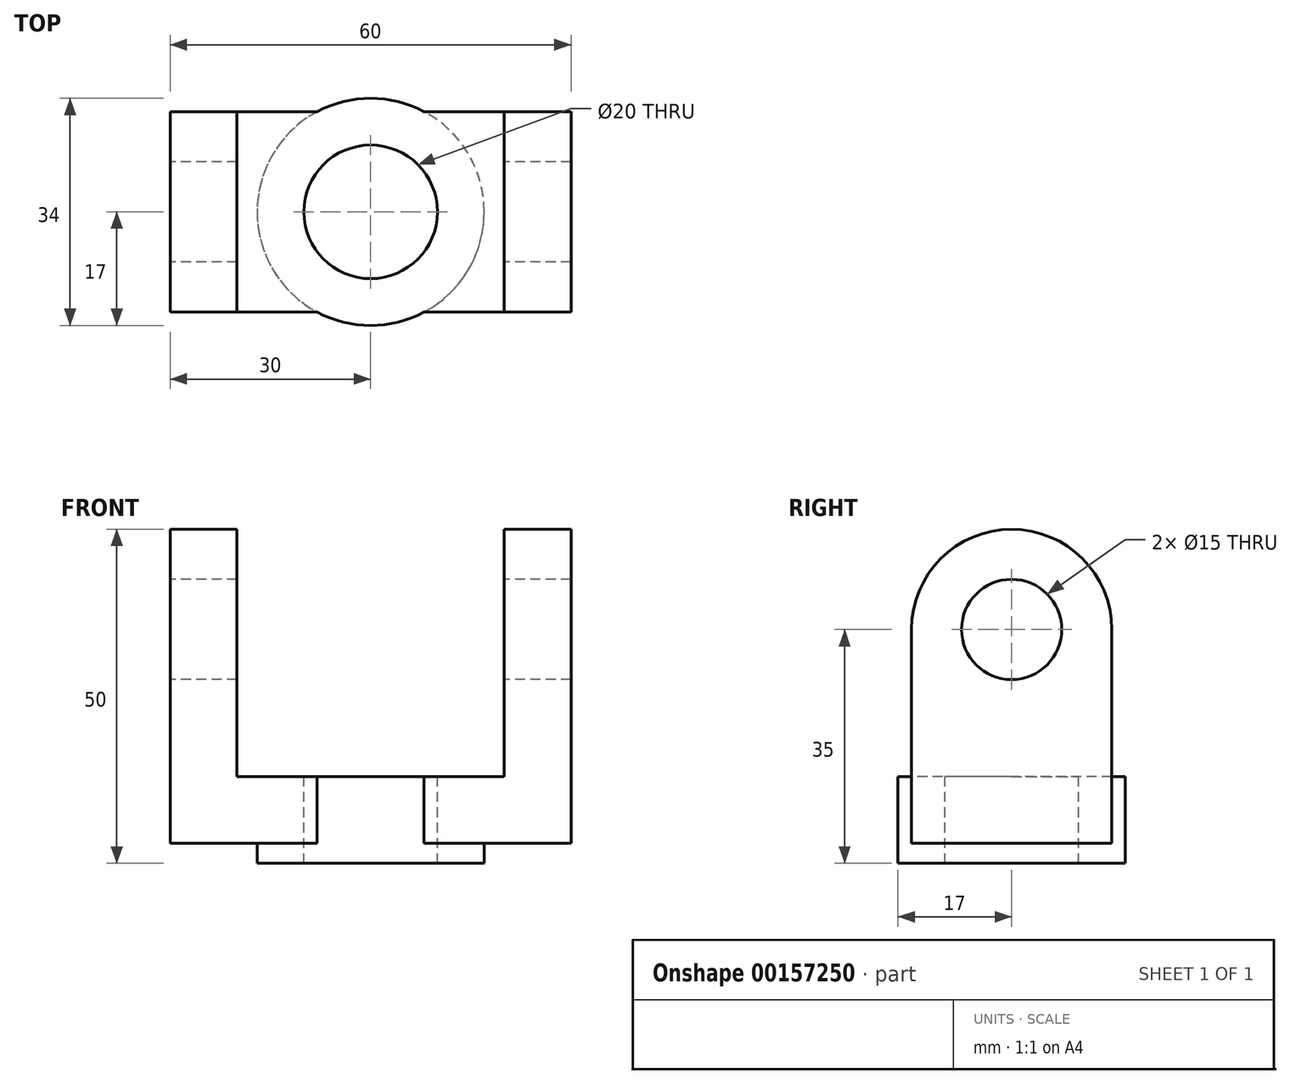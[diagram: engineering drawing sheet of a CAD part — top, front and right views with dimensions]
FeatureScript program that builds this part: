
annotation { "Feature Type Name" : "Feature", "Feature Type Description" : "" }
export const myFeature = defineFeature(function(context is Context, id is Id, definition is map)
    precondition{}
    {
        {
            var Q0;
            Q0=qCreatedBy(makeId("Right.planeOp"),FACE);
            var sketch = newSketch(context, id + "F0", { "sketchPlane" : qUnion([Q0])});
            skLineSegment(sketch, "E0", {"start": v(-15, 0) * mm, "end": v(15, 0) * mm});
            skLineSegment(sketch, "E1", {"start": v(-15, 0) * mm, "end": v(-15, 10) * mm});
            skLineSegment(sketch, "E2", {"start": v(15, 0) * mm, "end": v(15, 10) * mm});
            skLineSegment(sketch, "E3", {"start": v(-15, 10) * mm, "end": v(-15, 32) * mm});
            skLineSegment(sketch, "E4", {"start": v(15, 10) * mm, "end": v(15, 32) * mm});
            skArc(sketch, "E5", {"start": v(15, 32) * mm, "mid": v(0, 47) * mm, "end": v(-15, 32) * mm});
            skCircle(sketch, "E6", {"center": v(0, 32) * mm, "radius": 7.5 * mm});
            skSolve(sketch);
        }
        {
            var Q0;
            Q0 = qSketchRegion(id + "F0", true);
            extrude(context, id + "F1", {"entities" : qUnion([Q0]), "depth" : 60 * mm});
        }
        {
            var Q0;
            Q0=makeQuery(id+"F1.opExtrude","SWEPT_FACE",FACE,{"disambiguationData":[OSD([sQuery(id+"F0.wireOp",EDGE,"E3")])]});
            var sketch = newSketch(context, id + "F2", { "sketchPlane" : qUnion([Q0])});
            skLineSegment(sketch, "E7", {"start": v(10, 82.92) * mm, "end": v(10, 32) * mm});
            skLineSegment(sketch, "E8", {"start": v(10, 32) * mm, "end": v(50, 32) * mm});
            skLineSegment(sketch, "E9", {"start": v(50, 32) * mm, "end": v(50, 85.16) * mm});
            skLineSegment(sketch, "E10", {"start": v(50, 85.16) * mm, "end": v(10, 82.92) * mm});
            skSolve(sketch);
        }
        {
            var Q0;
            Q0 = qSketchRegion(id + "F2", true);
            extrude(context, id + "F3", {"entities" : qUnion([Q0]), "operationType" : NewBodyOperationType.REMOVE, "endBound" : BoundingType.THROUGH_ALL, "oppositeDirection" : true, "depth" : 25 * mm});
        }
        {
            var Q0;
            Q0=makeQuery(id+"F1.opExtrude","SWEPT_FACE",FACE,{"disambiguationData":[OSD([sQuery(id+"F0.wireOp",EDGE,"E1"),sQuery(id+"F0.wireOp",EDGE,"E3")])]});
            var sketch = newSketch(context, id + "F4", { "sketchPlane" : qUnion([Q0])});
            skLineSegment(sketch, "E11", {"start": v(50, 10) * mm, "end": v(50, 32) * mm});
            skLineSegment(sketch, "E12", {"start": v(50, 32) * mm, "end": v(10, 32) * mm});
            skLineSegment(sketch, "E13", {"start": v(10, 32) * mm, "end": v(10, 10) * mm});
            skLineSegment(sketch, "E14", {"start": v(10, 10) * mm, "end": v(50, 10) * mm});
            skSolve(sketch);
        }
        {
            var Q0;
            Q0 = qSketchRegion(id + "F4", true);
            extrude(context, id + "F5", {"entities" : qUnion([Q0]), "operationType" : NewBodyOperationType.REMOVE, "endBound" : BoundingType.THROUGH_ALL, "oppositeDirection" : true, "depth" : 25 * mm});
        }
        {
            var Q0;
            Q0=makeQuery(id+"F5.boolean.opBoolean","COPY",FACE,{"derivedFrom":makeQuery(id+"F5.opExtrude","SWEPT_FACE",FACE,{"disambiguationData":[OSD([sQuery(id+"F4.wireOp",EDGE,"E14")])]})});
            var sketch = newSketch(context, id + "F6", { "sketchPlane" : qUnion([Q0])});
            skCircle(sketch, "E15", {"center": v(30, 0) * mm, "radius": 10 * mm});
            skCircle(sketch, "E16", {"center": v(30, 0) * mm, "radius": 17 * mm});
            skSolve(sketch);
        }
        {
            var Q0;
            Q0 = qSketchRegion(id + "F6", true);
            extrude(context, id + "F7", {"entities" : qUnion([Q0]), "operationType" : NewBodyOperationType.ADD, "oppositeDirection" : true, "depth" : 13 * mm});
        }
        {
            var Q0;
            Q0=makeQuery(id+"F7.boolean.opBoolean","SPLIT",FACE,{"disambiguationData":[TD([makeQuery(id+"F7.opExtrude","SWEPT_FACE",FACE,{"disambiguationData":[OSD([sQuery(id+"F6.wireOp",EDGE,"E15")])]})])],"derivedFrom":makeQuery(id+"F1.opExtrude","SWEPT_FACE",FACE,{"disambiguationData":[OSD([sQuery(id+"F0.wireOp",EDGE,"E0")])]})});
            var sketch = newSketch(context, id + "F8", { "sketchPlane" : qUnion([Q0])});
            skCircle(sketch, "E17", {"center": v(30, 0) * mm, "radius": 10 * mm});
            skSolve(sketch);
        }
        {
            var Q0;
            Q0 = qSketchRegion(id + "F8", true);
            extrude(context, id + "F9", {"entities" : qUnion([Q0]), "operationType" : NewBodyOperationType.REMOVE, "endBound" : BoundingType.THROUGH_ALL, "oppositeDirection" : true, "depth" : 25 * mm});
        }
    });
